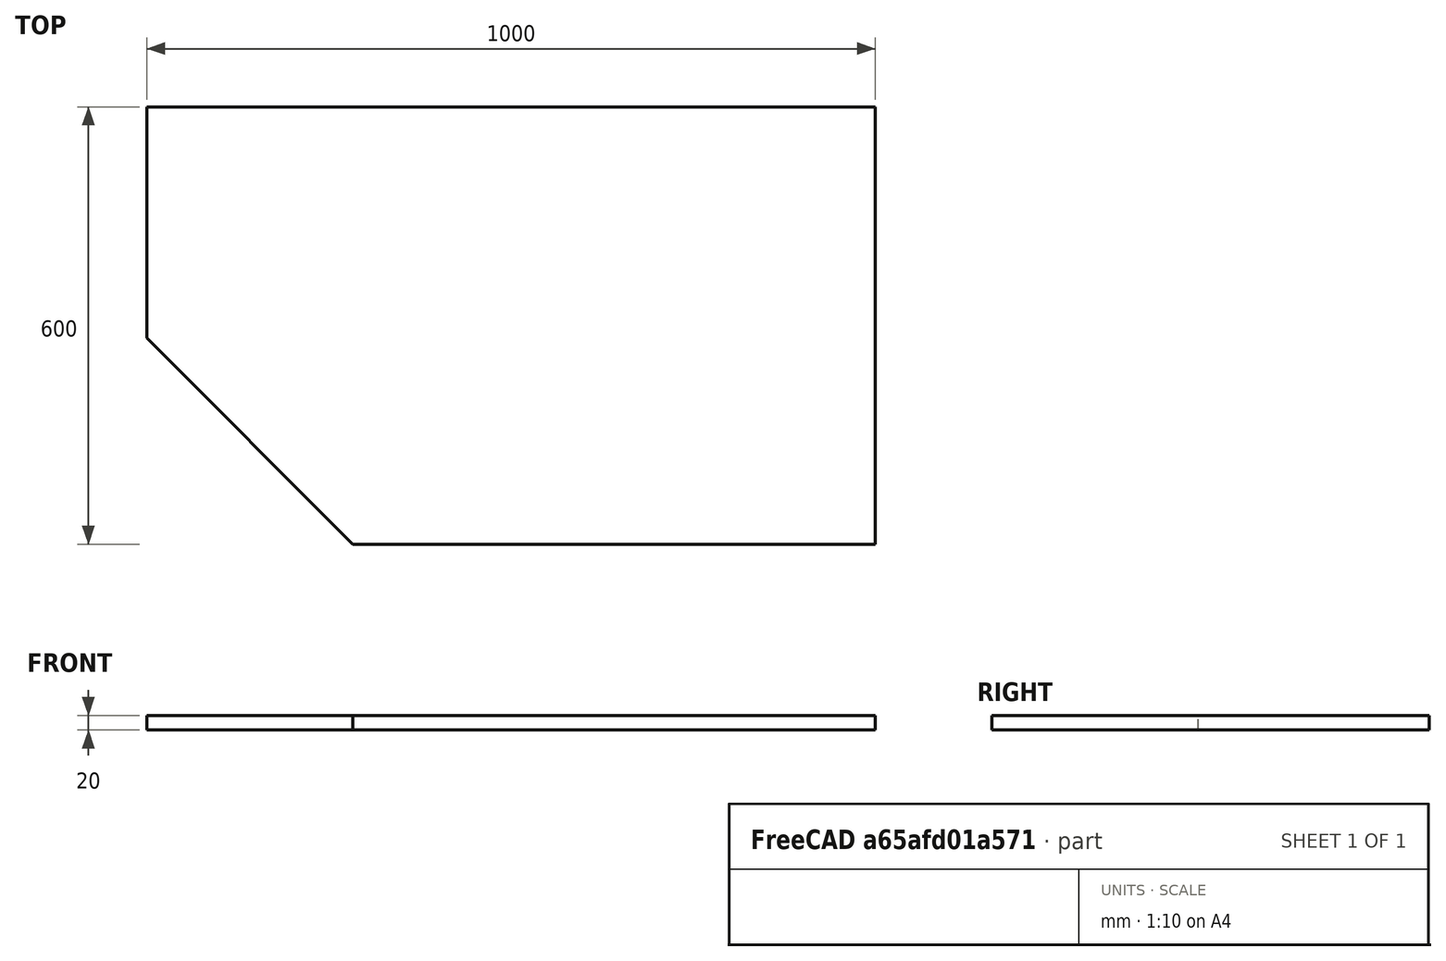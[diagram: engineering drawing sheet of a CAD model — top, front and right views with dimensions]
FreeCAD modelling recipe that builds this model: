
FCSTD DOCUMENT  (FreeCAD 0.18R4 (GitTag))
Label: TableBase
License: All rights reserved
LicenseURL: http://en.wikipedia.org/wiki/All_rights_reserved
objects: Sketcher::SketchObject×1, Part::Extrusion×1
note: 2 computed .brp shape members not serialized (recipe doc carries the construction recipe); baked Part::Feature solids carry a one-line shape summary decoded from their .brp

FEATURE [Sketcher::SketchObject] Sketch
  sketch-geometry (5):
    g0: LineSegment StartX=-500 StartY=300 StartZ=0 EndX=500 EndY=300 EndZ=0
    g1: LineSegment StartX=500 StartY=300 StartZ=0 EndX=500 EndY=-300 EndZ=0
    g2: LineSegment StartX=500 StartY=-300 StartZ=0 EndX=-217.157 EndY=-300 EndZ=0
    g3: LineSegment StartX=-217.157 StartY=-300 StartZ=0 EndX=-500 EndY=-17.1573 EndZ=0
    g4: LineSegment StartX=-500 StartY=-17.1573 StartZ=0 EndX=-500 EndY=300 EndZ=0
  constraints (15):
    c: Horizontal(g0)
    c: Coincident(g0,g1)
    c: Coincident(g2,g3)
    c: Coincident(g3,g4)
    c: Coincident(g4,g0)
    c: Vertical(g4)
    c: Vertical(g1)
    c: DistanceX(g0,g0) = 1000
    c: DistanceY(g2,g0) = 600
    c: DistanceY(g-1,g0) = 300
    c: Angle(g2,g3) = 2.35619
    c: Horizontal(g2)
    c: DistanceX(g0,g-1) = 500
    c: Distance(g3,g2) = 400
    c: Coincident(g2,g1)
FEATURE [Part::Extrusion] Extrude
  Base = -> Sketch
  Dir = (0,0,1)
  DirMode = 2
  FaceMakerClass = Part::FaceMakerBullseye
  LengthFwd = 20
  LengthRev = 0
  Solid = true
  Symmetric = false
